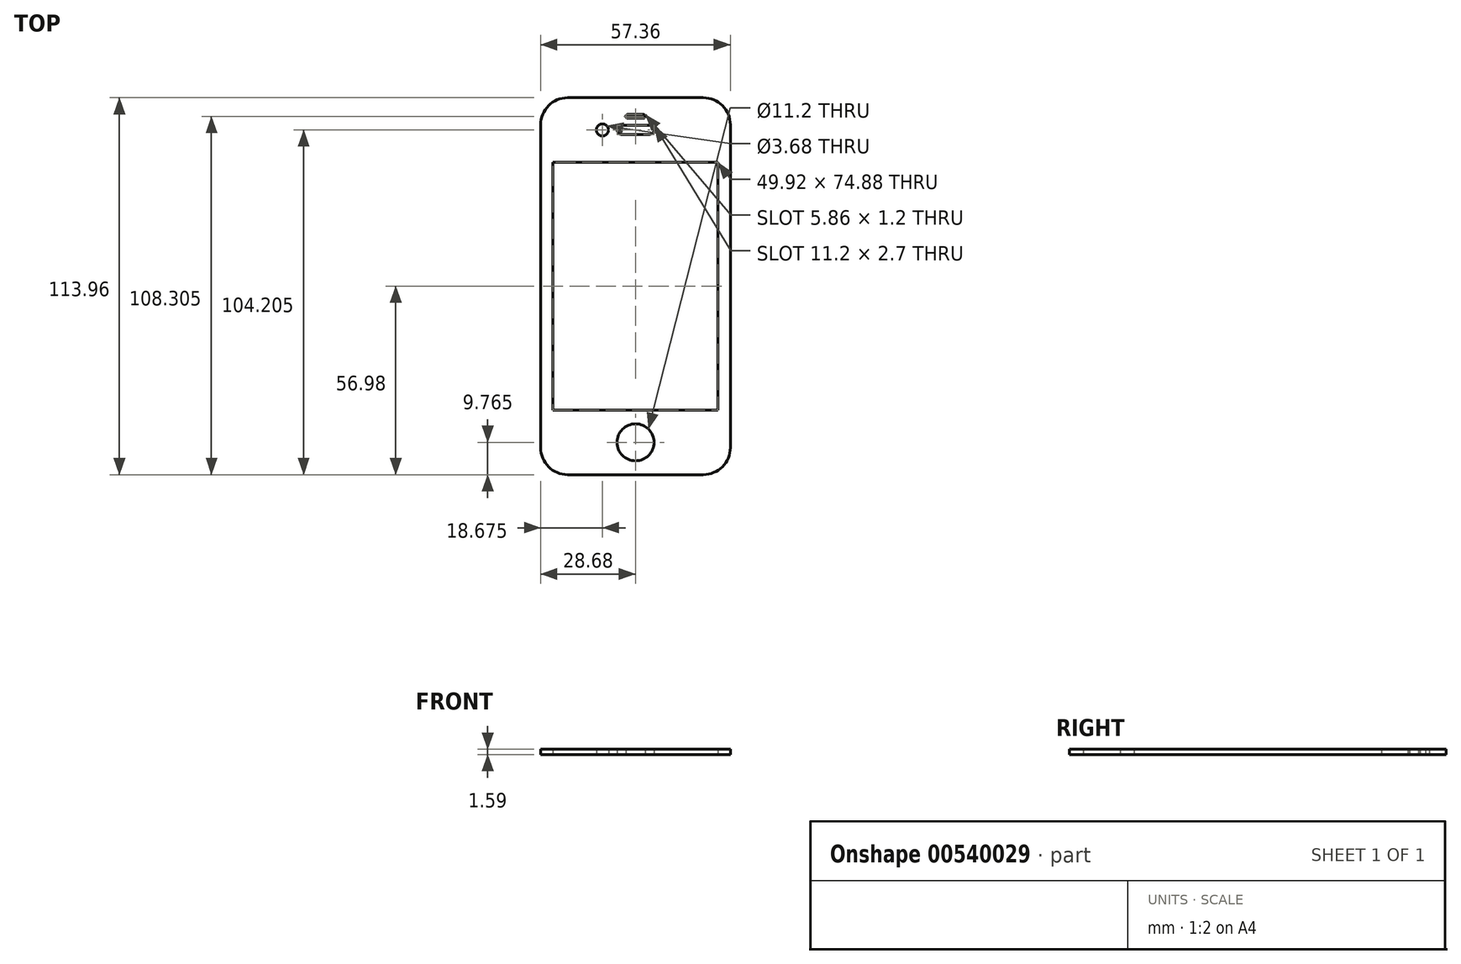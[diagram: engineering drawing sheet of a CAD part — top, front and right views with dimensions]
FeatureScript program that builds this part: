
annotation { "Feature Type Name" : "Feature", "Feature Type Description" : "" }
export const myFeature = defineFeature(function(context is Context, id is Id, definition is map)
    precondition{}
    {
        {
            var Q0;
            Q0=qCreatedBy(makeId("Top.planeOp"),FACE);
            var sketch = newSketch(context, id + "F0", { "sketchPlane" : qUnion([Q0])});
            skLineSegment(sketch, "E0.bottom", {"start": v(-20.5, 56.98) * mm, "end": v(20.5, 56.98) * mm});
            skLineSegment(sketch, "E0.top", {"start": v(-20.5, -56.98) * mm, "end": v(20.5, -56.98) * mm});
            skLineSegment(sketch, "E0.left", {"start": v(-28.67, 48.8) * mm, "end": v(-28.68, -48.8) * mm});
            skLineSegment(sketch, "E0.right", {"start": v(28.68, 48.8) * mm, "end": v(28.67, -48.8) * mm});
            skPoint(sketch, "E0.middle", {"position": v(0, 0) * mm});
            skPoint(sketch, "E1.visualSharp", {"position": v(-28.67, 56.98) * mm});
            skArc(sketch, "E1.filletArc", {"start": v(-20.5, 56.97) * mm, "mid": v(-26.28, 54.58) * mm, "end": v(-28.67, 48.8) * mm});
            skPoint(sketch, "E2.visualSharp", {"position": v(28.68, 56.98) * mm});
            skArc(sketch, "E2.filletArc", {"start": v(28.68, 48.8) * mm, "mid": v(26.28, 54.58) * mm, "end": v(20.5, 56.97) * mm});
            skPoint(sketch, "E3.visualSharp", {"position": v(-28.68, -56.98) * mm});
            skArc(sketch, "E3.filletArc", {"start": v(-28.68, -48.8) * mm, "mid": v(-26.28, -54.58) * mm, "end": v(-20.5, -56.97) * mm});
            skPoint(sketch, "E4.visualSharp", {"position": v(28.67, -56.98) * mm});
            skArc(sketch, "E4.filletArc", {"start": v(20.5, -56.97) * mm, "mid": v(26.28, -54.58) * mm, "end": v(28.67, -48.8) * mm});
            skCircle(sketch, "E5", {"center": v(0, -47.22) * mm, "radius": 5.6 * mm});
            skLineSegment(sketch, "E6.bottom", {"start": v(4.25, 45.88) * mm, "end": v(-4.25, 45.88) * mm});
            skLineSegment(sketch, "E6.top", {"start": v(4.25, 48.58) * mm, "end": v(-4.25, 48.58) * mm});
            skLineSegment(sketch, "E6.left", {"start": v(5.6, 47.23) * mm, "end": v(5.6, 47.23) * mm});
            skLineSegment(sketch, "E6.right", {"start": v(-5.6, 47.23) * mm, "end": v(-5.6, 47.23) * mm});
            skPoint(sketch, "E6.middle", {"position": v(0, 47.23) * mm});
            skPoint(sketch, "E7.visualSharp", {"position": v(-5.6, 48.58) * mm});
            skArc(sketch, "E7.filletArc", {"start": v(-4.25, 48.58) * mm, "mid": v(-5.2, 48.18) * mm, "end": v(-5.6, 47.23) * mm});
            skPoint(sketch, "E8.visualSharp", {"position": v(-5.6, 45.88) * mm});
            skArc(sketch, "E8.filletArc", {"start": v(-5.6, 47.23) * mm, "mid": v(-5.2, 46.27) * mm, "end": v(-4.25, 45.88) * mm});
            skPoint(sketch, "E9.visualSharp", {"position": v(5.6, 45.88) * mm});
            skArc(sketch, "E9.filletArc", {"start": v(4.25, 45.88) * mm, "mid": v(5.2, 46.27) * mm, "end": v(5.6, 47.23) * mm});
            skPoint(sketch, "E10.visualSharp", {"position": v(5.6, 48.58) * mm});
            skArc(sketch, "E10.filletArc", {"start": v(5.6, 47.23) * mm, "mid": v(5.2, 48.18) * mm, "end": v(4.25, 48.58) * mm});
            skPoint(sketch, "E11.endSnap0", {"position": v(0, 45.88) * mm});
            skPoint(sketch, "E12.middle", {"position": v(0, 51.33) * mm});
            skLineSegment(sketch, "E13.left", {"start": v(2.93, 51.33) * mm, "end": v(2.93, 51.33) * mm});
            skLineSegment(sketch, "E14.MirrorCS", {"start": v(-2.93, 51.33) * mm, "end": v(-2.93, 51.33) * mm});
            skLineSegment(sketch, "E15", {"start": v(-2.33, 51.93) * mm, "end": v(2.33, 51.93) * mm});
            skLineSegment(sketch, "E16", {"start": v(2.33, 50.73) * mm, "end": v(-2.33, 50.73) * mm});
            skPoint(sketch, "E17.visualSharp", {"position": v(-2.93, 51.93) * mm});
            skArc(sketch, "E17.filletArc", {"start": v(-2.33, 51.93) * mm, "mid": v(-2.75, 51.75) * mm, "end": v(-2.93, 51.33) * mm});
            skPoint(sketch, "E18.visualSharp", {"position": v(-2.93, 50.73) * mm});
            skArc(sketch, "E18.filletArc", {"start": v(-2.93, 51.33) * mm, "mid": v(-2.75, 50.9) * mm, "end": v(-2.33, 50.73) * mm});
            skPoint(sketch, "E19.visualSharp", {"position": v(2.93, 51.93) * mm});
            skArc(sketch, "E19.filletArc", {"start": v(2.93, 51.33) * mm, "mid": v(2.75, 51.75) * mm, "end": v(2.33, 51.93) * mm});
            skPoint(sketch, "E20.visualSharp", {"position": v(2.93, 50.73) * mm});
            skArc(sketch, "E20.filletArc", {"start": v(2.33, 50.73) * mm, "mid": v(2.75, 50.9) * mm, "end": v(2.93, 51.33) * mm});
            skLineSegment(sketch, "E21.bottom", {"start": v(-24.96, 37.44) * mm, "end": v(24.96, 37.44) * mm});
            skLineSegment(sketch, "E21.top", {"start": v(-24.96, -37.44) * mm, "end": v(24.96, -37.44) * mm});
            skLineSegment(sketch, "E21.left", {"start": v(-24.96, 37.44) * mm, "end": v(-24.96, -37.44) * mm});
            skLineSegment(sketch, "E21.right", {"start": v(24.96, 37.44) * mm, "end": v(24.96, -37.44) * mm});
            skCircle(sketch, "E22", {"center": v(-10, 47.23) * mm, "radius": 1.84 * mm});
            skSolve(sketch);
        }
        {
            var Q0;
            Q0=makeQuery(id+"F0.imprint","IMPRINT",FACE,{"disambiguationData":[TD([[makeQuery(id+"F0.imprint","IMPRINT",EDGE,{"derivedFrom":sQuery(id+"F0.wireOp",EDGE,"E0.bottom")}),-1.0]])]});
            extrude(context, id + "F1", {"entities" : qUnion([Q0]), "depth" : 1.59 * mm, "offsetDistance" : 25 * mm});
        }
        {
            var Q0;
            Q0=makeQuery(id+"F0.imprint","IMPRINT",FACE,{"disambiguationData":[TD([[makeQuery(id+"F0.imprint","IMPRINT",EDGE,{"derivedFrom":sQuery(id+"F0.wireOp",EDGE,"E21.bottom")}),-1.0]])]});
            extrude(context, id + "F2", {"entities" : qUnion([Q0]), "depth" : 1.59 * mm, "offsetDistance" : 25 * mm});
        }
        {
            var Q0;
            Q0=makeQuery(id+"F0.imprint","IMPRINT",FACE,{"disambiguationData":[TD([[makeQuery(id+"F0.imprint","IMPRINT",EDGE,{"derivedFrom":sQuery(id+"F0.wireOp",EDGE,"E6.bottom")}),-1.0]])]});
            var Q1;
            Q1=makeQuery(id+"F0.imprint","IMPRINT",FACE,{"disambiguationData":[TD([[makeQuery(id+"F0.imprint","IMPRINT",EDGE,{"derivedFrom":sQuery(id+"F0.wireOp",EDGE,"E15")}),-1.0]])]});
            extrude(context, id + "F3", {"entities" : qUnion([Q0, Q1]), "depth" : 1.57 * mm, "offsetDistance" : 25 * mm});
        }
        {
            var Q0;
            Q0=makeQuery(id+"F0.imprint","IMPRINT",FACE,{"disambiguationData":[TD([[makeQuery(id+"F0.imprint","IMPRINT",EDGE,{"derivedFrom":sQuery(id+"F0.wireOp",EDGE,"E22")}),1.0]])]});
            extrude(context, id + "F4", {"entities" : qUnion([Q0]), "depth" : 1.59 * mm, "offsetDistance" : 25 * mm});
        }
        {
            var Q0;
            Q0=makeQuery(id+"F0.imprint","IMPRINT",FACE,{"disambiguationData":[TD([[makeQuery(id+"F0.imprint","IMPRINT",EDGE,{"derivedFrom":sQuery(id+"F0.wireOp",EDGE,"E5")}),1.0]])]});
            extrude(context, id + "F5", {"entities" : qUnion([Q0]), "depth" : 1.57 * mm, "offsetDistance" : 25 * mm});
        }
    });
